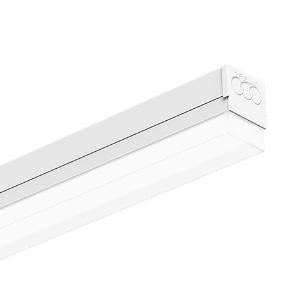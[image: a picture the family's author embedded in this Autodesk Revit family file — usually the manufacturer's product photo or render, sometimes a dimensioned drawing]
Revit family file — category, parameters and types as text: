
# Revit family: 3f_filippi_-_3f_zeta_dr_3f_filippi_-_10881_-_3f_zeta_dr_2x18_led_l1194
name_source: partatom
category: Lighting Fixtures
units: mm (PartAtom-declared; Revit-internal decimal feet)

## family parameters
Cut with Voids When Loaded = No
Host = Face
Light Source = No
Part Type = Normal
Room Calculation Point = No
Round Connector Dimension = Use Diameter
Shared = No

## types (1)
- 3F Filippi - 3F Zeta DR (1 x LED, 4851 lm, 40 W, 4000 K)
    Apparent Load = 40 VA
    Approval mark = CE
    CIE Flux Codes = 41 72 91 86 100
    Color Rendering = 80
    Color Temperature = 4000 K
    Control Gear = Electronic ballast
    Default Elevation = 1800 mm
    Description = ILLUMINOTECHNICAL
Luminous efficiency 100% (DLOR 86%, ULOR 14%).
Initial luminous flux of the luminaire 4851 lm.
Diffused symmetric distribution.
Installation Interdistance Transv.D = 1.31 x hu - Long.D = 1.25 x hu.
Tabular UGR (CIE 117 - 4H-8H; S=0.25H; 70/50/20): RUG 25.5 - 24.1.
Beam angle: 136° - 112°.
Luminous efficacy 121 lm/W.
Lifetime (L93/B10): 30000 h. (tq+25°C)
Lifetime (L90/B10): 50000 h. (tq+25°C)
Lifetime (L85/B10): 80000 h. (tq+25°C)
Lifetime (L80/B10): 100000 h. (tq+25°C)
Sudden decreased luminous flux after 50000 hours: 0% (C0).
Photobiological safety in compliance with IEC/TR 62778: RG0 risk exempt, (IEC 62471).
In compliance with IEC/EN 62722-2-1 - IEC/EN 62717 standards.

SOURCE
2 linear LED modules 18W/840.
Energy efficiency class (UE 2019/2020 - UE 2019/2015): D.
CIE 13.3 Colour rendering index: CRI >80 (R9 <50%).
IES TM-30 Fidelity Index: Rf = 84 Rg = 95.
CCT nominal colour temperature 4000 K.
Colour initial tolerance (MacAdam): SDCM 3.

MECHANICAL
Housing in hot-galvanised steel, painted in white polyester, obtained through rolling process.
Light unit in hot-galvanised steel, painted in white polyester base with fixing springs and retractable safety hooks in stainless steel.
Rectangular screen in self-extinguishing polycarbonate, UV stabilised, opal, with smooth outer surface.
End caps in white polycarbonate.
Pair of stainless steel sliding brackets with sliding block screws.
Luminaire with limited surface temperature. - D - (EN 60598-2-24)
Dimensions: 1194x62 mm, height 81 mm. Weight 2.87 kg.
IP40 protection degree.
Mechanical strength to impacts IK06 (1 joule).
Glow-wire test resistance 850°C.

ELECTRICAL
Halogen Free electronic wiring 230V-50/60Hz, power factor 0.95, THD <25%, constant output current, SELV, class I, 1 driver.
Power of the luminaire 40 W.
ENEC - CE.
SAFE FLICKER: PstLM=<1 and SVM=<0.4 (IEC TR 61547-1 and IEC TR 63158), to ensure a more comfortable and safe light.
Luminaire compliant with EN 60598-2-22 for power supply from a centralised emergency system CPSS (Central Power Supply System), not incorporated in the luminaire - high risk areas excluded. The default power and flux are 100% in AC and 100% in DC.
Ambient temperature from 0°C to +25°C.
Temperature class T6 max 85°C.
Relative humidity UR: <85%.

INSTALLATION
Ceiling / Suspended / Wall.
All accessories dedicated to this product are available on the Catalog and on our website www.3F-Filippi.com.

APPLICATIONS
Suitable product for food production plants (HACCP), IFS (Food Version 6), BRC (GSFS Food Version 7).
In commercial environments, exhibition areas, shops and stores.

WARNING
Luminaire designed for disposal/recycling at end-of-life.
Replaceable (LED only) light source by a professional. Replaceable control gear by a professional.
    Height = 81 mm
    Lamp = 1 x LED
    Lamp Light Flux = 4851 lm
    Lamp Power = 40 W
    Lamp count = 1
    Length = 1194 mm
    Lifetime = 50000 h
    Luminous efficacy = 121 lm/W
    Manufacturer = 3F Filippi
    ModVariant = No
    Model = 3F Filippi - 10881 - 3F Zeta DR 2x18 LED L1194
    Mounting Place = Ceiling
    Mounting Type = Pendant
    Number of Poles = 1
    OnlyDefault = Yes
    Power Factor = 1
    Product Name = 3F Filippi - 3F Zeta DR
    Product group = pendant luminaire
    ProductGroupID = 9
    Protection Class = Protection class I
    Protection Degree = IP 40
    RLX_Detail_Level = 1
    RLX_Emergency_Light_Flux = 0 lm
    RLX_Emergency_Type = 0
    RLX_Emergency_Type_DB = No
    RlxData = <blob elided: 33025 chars, md5=20c47165>
    Socket = socket
    Standby Power = 0 W
    System Light Flux = 4851 lm
    System Power = 40 W
    Type Comments = Product without accessories
    Type Image = 3ffilippi_3f_zeta_dr.jpg
    URL = http://relux.com
    VarID = ---
    Voltage = 0 V
    Weight = 0.00 kg
    Width = 62 mm  [stored 0.203412 ft]

note: [stored X ft] marks values corroborated as IEEE doubles in the binary element streams (Revit-internal decimal feet)

## geometry (parser evidence)
native form markers: Blend x4, Sweep x14
no freeform markers — native parametric forms only
